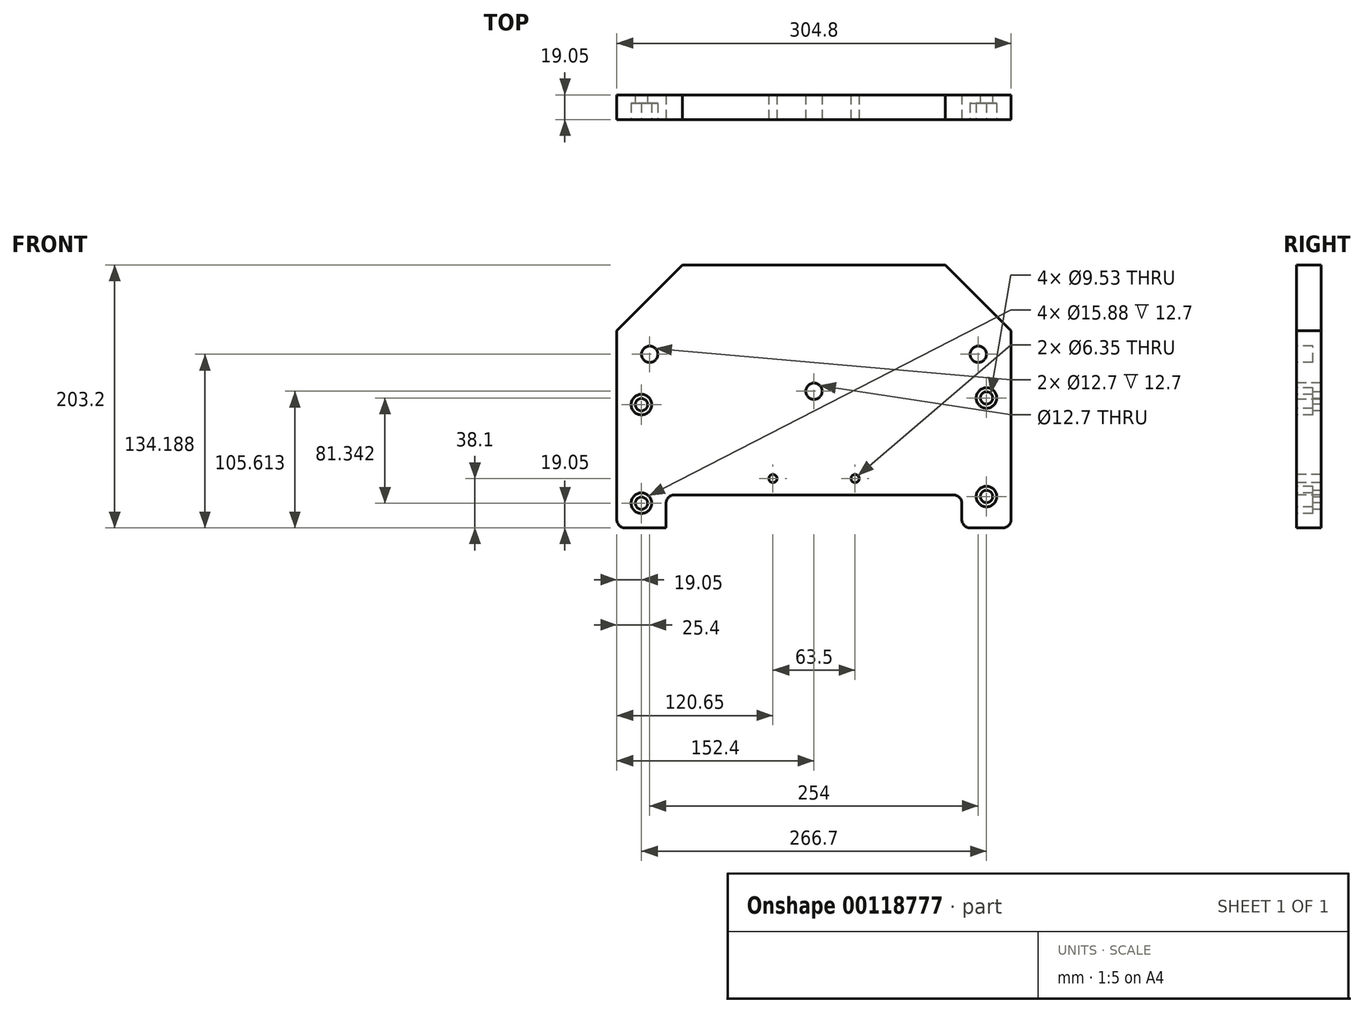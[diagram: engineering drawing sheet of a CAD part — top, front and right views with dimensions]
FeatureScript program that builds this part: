
annotation { "Feature Type Name" : "Feature", "Feature Type Description" : "" }
export const myFeature = defineFeature(function(context is Context, id is Id, definition is map)
    precondition{}
    {
        {
            var Q0;
            Q0=qCreatedBy(makeId("Front.planeOp"),FACE);
            var sketch = newSketch(context, id + "F0", { "sketchPlane" : qUnion([Q0])});
            skLineSegment(sketch, "E0.bottom", {"start": v(0, 0) * mm, "end": v(304.8, 0) * mm});
            skLineSegment(sketch, "E0.top", {"start": v(0, 203.2) * mm, "end": v(304.8, 203.2) * mm});
            skLineSegment(sketch, "E0.left", {"start": v(0, 0) * mm, "end": v(0, 203.2) * mm});
            skLineSegment(sketch, "E0.right", {"start": v(304.8, 0) * mm, "end": v(304.8, 203.2) * mm});
            skSolve(sketch);
        }
        {
            var Q0;
            Q0 = qSketchRegion(id + "F0", true);
            extrude(context, id + "F1", {"entities" : qUnion([Q0]), "depth" : 19.05 * mm});
        }
        {
            var Q0;
            Q0=makeQuery(id+"F1.opExtrude","CAP_FACE",FACE,{"disambiguationData":[OSD([sQuery(id+"F0.wireOp",EDGE,"E0.bottom"),sQuery(id+"F0.wireOp",EDGE,"E0.top"),sQuery(id+"F0.wireOp",EDGE,"E0.left"),sQuery(id+"F0.wireOp",EDGE,"E0.right")])],"isStart":false});
            var sketch = newSketch(context, id + "F2", { "sketchPlane" : qUnion([Q0])});
            skPoint(sketch, "E1", {"position": v(38.1, 25.4) * mm});
            skPoint(sketch, "E2", {"position": v(266.7, 25.4) * mm});
            skLineSegment(sketch, "E3", {"start": v(38.1, 25.4) * mm, "end": v(38.1, 0) * mm});
            skLineSegment(sketch, "E4", {"start": v(266.7, 25.4) * mm, "end": v(38.1, 25.4) * mm});
            skLineSegment(sketch, "E5", {"start": v(266.7, 25.4) * mm, "end": v(266.7, 0) * mm});
            skSolve(sketch);
        }
        {
            var Q0;
            Q0 = qSketchRegion(id + "F2", true);
            var Q1;
            {var subQ0=sQuery(id+"F2.wireOp",EDGE,"E3");Q1=makeQuery(id+"F2.imprint","IMPRINT",FACE,{"disambiguationData":[TD([[makeQuery(id+"F2.imprint","IMPRINT",EDGE,{"derivedFrom":subQ0}),1.0]])]});}
            extrude(context, id + "F3", {"entities" : qUnion([Q0, Q1]), "operationType" : NewBodyOperationType.REMOVE, "endBound" : BoundingType.THROUGH_ALL, "oppositeDirection" : true, "depth" : 25.4 * mm});
        }
        {
            var Q0;
            Q0=makeQuery(id+"F1.opExtrude","CAP_FACE",FACE,{"disambiguationData":[OSD([sQuery(id+"F0.wireOp",EDGE,"E0.bottom"),sQuery(id+"F0.wireOp",EDGE,"E0.top"),sQuery(id+"F0.wireOp",EDGE,"E0.left"),sQuery(id+"F0.wireOp",EDGE,"E0.right")])],"isStart":false});
            var sketch = newSketch(context, id + "F4", { "sketchPlane" : qUnion([Q0])});
            skLineSegment(sketch, "E6", {"start": v(152.4, 25.4) * mm, "end": v(152.4, 203.2) * mm, "construction": true});
            skPoint(sketch, "E7", {"position": v(120.65, 38.1) * mm});
            skPoint(sketch, "E8", {"position": v(184.15, 38.1) * mm});
            skSolve(sketch);
        }
        {
            var Q0;
            Q0=sQuery(id+"F4.wireOp",VERTEX,"E7");
            var Q1;
            Q1=sQuery(id+"F4.wireOp",VERTEX,"E8");
            var Q2;
            Q2=makeQuery(id+"F1.opExtrude","SWEPT_BODY",BODY,{"disambiguationData":[OSD([sQuery(id+"F0.wireOp",EDGE,"E0.bottom"),sQuery(id+"F0.wireOp",EDGE,"E0.top"),sQuery(id+"F0.wireOp",EDGE,"E0.left"),sQuery(id+"F0.wireOp",EDGE,"E0.right")])]});
            hole(context, id + "F5", {"style" : HoleStyle.SIMPLE, "endStyle" : HoleEndStyle.THROUGH, "holeDiameter" : 6.35 * mm, "locations" : qUnion([Q0, Q1]), "scope" : qUnion([Q2]), "isTappedThrough" : true});
        }
        {
            var Q0;
            Q0=makeQuery(id+"F3.boolean.opBoolean","COPY",EDGE,{"derivedFrom":makeQuery(id+"F3.opExtrude","SWEPT_EDGE",EDGE,{"disambiguationData":[OSD([sQuery(id+"F0.wireOp",EDGE,"E0.bottom"),sQuery(id+"F2.wireOp",EDGE,"E3")])]})});
            var Q1;
            Q1=makeQuery(id+"F3.boolean.opBoolean","COPY",EDGE,{"derivedFrom":makeQuery(id+"F3.opExtrude","SWEPT_EDGE",EDGE,{"disambiguationData":[OSD([sQuery(id+"F2.wireOp",EDGE,"E3"),sQuery(id+"F2.wireOp",EDGE,"E4")])]})});
            var Q2;
            Q2=makeQuery(id+"F1.opExtrude","SWEPT_EDGE",EDGE,{"disambiguationData":[OSD([sQuery(id+"F0.wireOp",EDGE,"E0.bottom"),sQuery(id+"F0.wireOp",EDGE,"E0.left")])]});
            var Q3;
            Q3=makeQuery(id+"F3.boolean.opBoolean","COPY",EDGE,{"derivedFrom":makeQuery(id+"F3.opExtrude","SWEPT_EDGE",EDGE,{"disambiguationData":[OSD([sQuery(id+"F2.wireOp",EDGE,"E4"),sQuery(id+"F2.wireOp",EDGE,"E5")])]})});
            var Q4;
            Q4=makeQuery(id+"F3.boolean.opBoolean","COPY",EDGE,{"derivedFrom":makeQuery(id+"F3.opExtrude","SWEPT_EDGE",EDGE,{"disambiguationData":[OSD([sQuery(id+"F0.wireOp",EDGE,"E0.bottom"),sQuery(id+"F2.wireOp",EDGE,"E5")])]})});
            var Q5;
            Q5=makeQuery(id+"F1.opExtrude","SWEPT_EDGE",EDGE,{"disambiguationData":[OSD([sQuery(id+"F0.wireOp",EDGE,"E0.bottom"),sQuery(id+"F0.wireOp",EDGE,"E0.right")])]});
            fillet(context, id + "F6", {"entities" : qUnion([Q0, Q1, Q2, Q3, Q4, Q5]), "radius" : 6.35 * mm, "tangentPropagation" : true, "allowEdgeOverflow" : false});
        }
        {
            var Q0;
            Q0=makeQuery(id+"F1.opExtrude","CAP_FACE",FACE,{"disambiguationData":[OSD([sQuery(id+"F0.wireOp",EDGE,"E0.bottom"),sQuery(id+"F0.wireOp",EDGE,"E0.top"),sQuery(id+"F0.wireOp",EDGE,"E0.left"),sQuery(id+"F0.wireOp",EDGE,"E0.right")])],"isStart":false});
            var sketch = newSketch(context, id + "F7", { "sketchPlane" : qUnion([Q0])});
            skPoint(sketch, "E9", {"position": v(152.4, 105.61) * mm});
            skPoint(sketch, "E9.positionSnap0", {"position": v(152.4, 25.4) * mm});
            skSolve(sketch);
        }
        {
            var Q0;
            Q0=sQuery(id+"F7.wireOp",VERTEX,"E9");
            var Q1;
            Q1=makeQuery(id+"F1.opExtrude","SWEPT_BODY",BODY,{"disambiguationData":[OSD([sQuery(id+"F0.wireOp",EDGE,"E0.bottom"),sQuery(id+"F0.wireOp",EDGE,"E0.top"),sQuery(id+"F0.wireOp",EDGE,"E0.left"),sQuery(id+"F0.wireOp",EDGE,"E0.right")])]});
            hole(context, id + "F8", {"style" : HoleStyle.SIMPLE, "endStyle" : HoleEndStyle.THROUGH, "holeDiameter" : 12.7 * mm, "locations" : qUnion([Q0]), "scope" : qUnion([Q1]), "isTappedThrough" : true});
        }
        {
            var Q0;
            Q0=makeQuery(id+"F1.opExtrude","CAP_FACE",FACE,{"disambiguationData":[OSD([sQuery(id+"F0.wireOp",EDGE,"E0.bottom"),sQuery(id+"F0.wireOp",EDGE,"E0.top"),sQuery(id+"F0.wireOp",EDGE,"E0.left"),sQuery(id+"F0.wireOp",EDGE,"E0.right")])],"isStart":false});
            var sketch = newSketch(context, id + "F9", { "sketchPlane" : qUnion([Q0])});
            skPoint(sketch, "E10", {"position": v(152.4, 134.19) * mm});
            skPoint(sketch, "E10.positionSnap0", {"position": v(152.4, 203.2) * mm});
            skPoint(sketch, "E11", {"position": v(152.4, 105.61) * mm});
            skPoint(sketch, "E12", {"position": v(25.4, 134.19) * mm});
            skPoint(sketch, "E13", {"position": v(279.4, 134.19) * mm});
            skCircle(sketch, "E14", {"center": v(25.4, 134.19) * mm, "radius": 6.35 * mm});
            skCircle(sketch, "E15", {"center": v(279.4, 134.19) * mm, "radius": 6.35 * mm});
            skSolve(sketch);
        }
        {
            var Q0;
            Q0=makeQuery(id+"F9.imprint","IMPRINT",FACE,{"disambiguationData":[TD([[makeQuery(id+"F9.imprint","IMPRINT",EDGE,{"derivedFrom":sQuery(id+"F9.wireOp",EDGE,"E14")}),1.0]])]});
            var Q1;
            Q1=makeQuery(id+"F9.imprint","IMPRINT",FACE,{"disambiguationData":[TD([[makeQuery(id+"F9.imprint","IMPRINT",EDGE,{"derivedFrom":sQuery(id+"F9.wireOp",EDGE,"E15")}),1.0]])]});
            extrude(context, id + "F10", {"entities" : qUnion([Q0, Q1]), "operationType" : NewBodyOperationType.REMOVE, "oppositeDirection" : true, "depth" : 12.7 * mm});
        }
        {
            var Q0;
            Q0=makeQuery(id+"F1.opExtrude","CAP_FACE",FACE,{"disambiguationData":[OSD([sQuery(id+"F0.wireOp",EDGE,"E0.bottom"),sQuery(id+"F0.wireOp",EDGE,"E0.top"),sQuery(id+"F0.wireOp",EDGE,"E0.left"),sQuery(id+"F0.wireOp",EDGE,"E0.right")])],"isStart":false});
            var sketch = newSketch(context, id + "F11", { "sketchPlane" : qUnion([Q0])});
            skPoint(sketch, "E16", {"position": v(19.05, 19.05) * mm});
            skPoint(sketch, "E16.positionSnap0", {"position": v(19.05, 0) * mm});
            skPoint(sketch, "E17", {"position": v(285.75, 24.2) * mm});
            skPoint(sketch, "E17.positionSnap0", {"position": v(285.75, 0) * mm});
            skPoint(sketch, "E18", {"position": v(19.05, 95.25) * mm});
            skPoint(sketch, "E19", {"position": v(285.75, 100.4) * mm});
            skSolve(sketch);
        }
        {
            var Q0;
            Q0=sQuery(id+"F11.wireOp",VERTEX,"E18");
            var Q1;
            Q1=sQuery(id+"F11.wireOp",VERTEX,"E19");
            var Q2;
            Q2=sQuery(id+"F11.wireOp",VERTEX,"E17");
            var Q3;
            Q3=sQuery(id+"F11.wireOp",VERTEX,"E16");
            var Q4;
            Q4=makeQuery(id+"F1.opExtrude","SWEPT_BODY",BODY,{"disambiguationData":[OSD([sQuery(id+"F0.wireOp",EDGE,"E0.bottom"),sQuery(id+"F0.wireOp",EDGE,"E0.top"),sQuery(id+"F0.wireOp",EDGE,"E0.left"),sQuery(id+"F0.wireOp",EDGE,"E0.right")])]});
            hole(context, id + "F12", {"style" : HoleStyle.C_BORE, "endStyle" : HoleEndStyle.THROUGH, "holeDiameter" : 9.52 * mm, "cBoreDiameter" : 15.88 * mm, "cBoreDepth" : 12.7 * mm, "locations" : qUnion([Q0, Q1, Q2, Q3]), "scope" : qUnion([Q4]), "isTappedThrough" : true});
        }
        {
            var Q0;
            Q0=makeQuery(id+"F1.opExtrude","SWEPT_EDGE",EDGE,{"disambiguationData":[OSD([sQuery(id+"F0.wireOp",EDGE,"E0.top"),sQuery(id+"F0.wireOp",EDGE,"E0.left")])]});
            var Q1;
            Q1=makeQuery(id+"F1.opExtrude","SWEPT_EDGE",EDGE,{"disambiguationData":[OSD([sQuery(id+"F0.wireOp",EDGE,"E0.top"),sQuery(id+"F0.wireOp",EDGE,"E0.right")])]});
            chamfer(context, id + "F13", {"entities" : qUnion([Q0, Q1]), "width" : 50.8 * mm, "tangentPropagation" : true});
        }
    });
